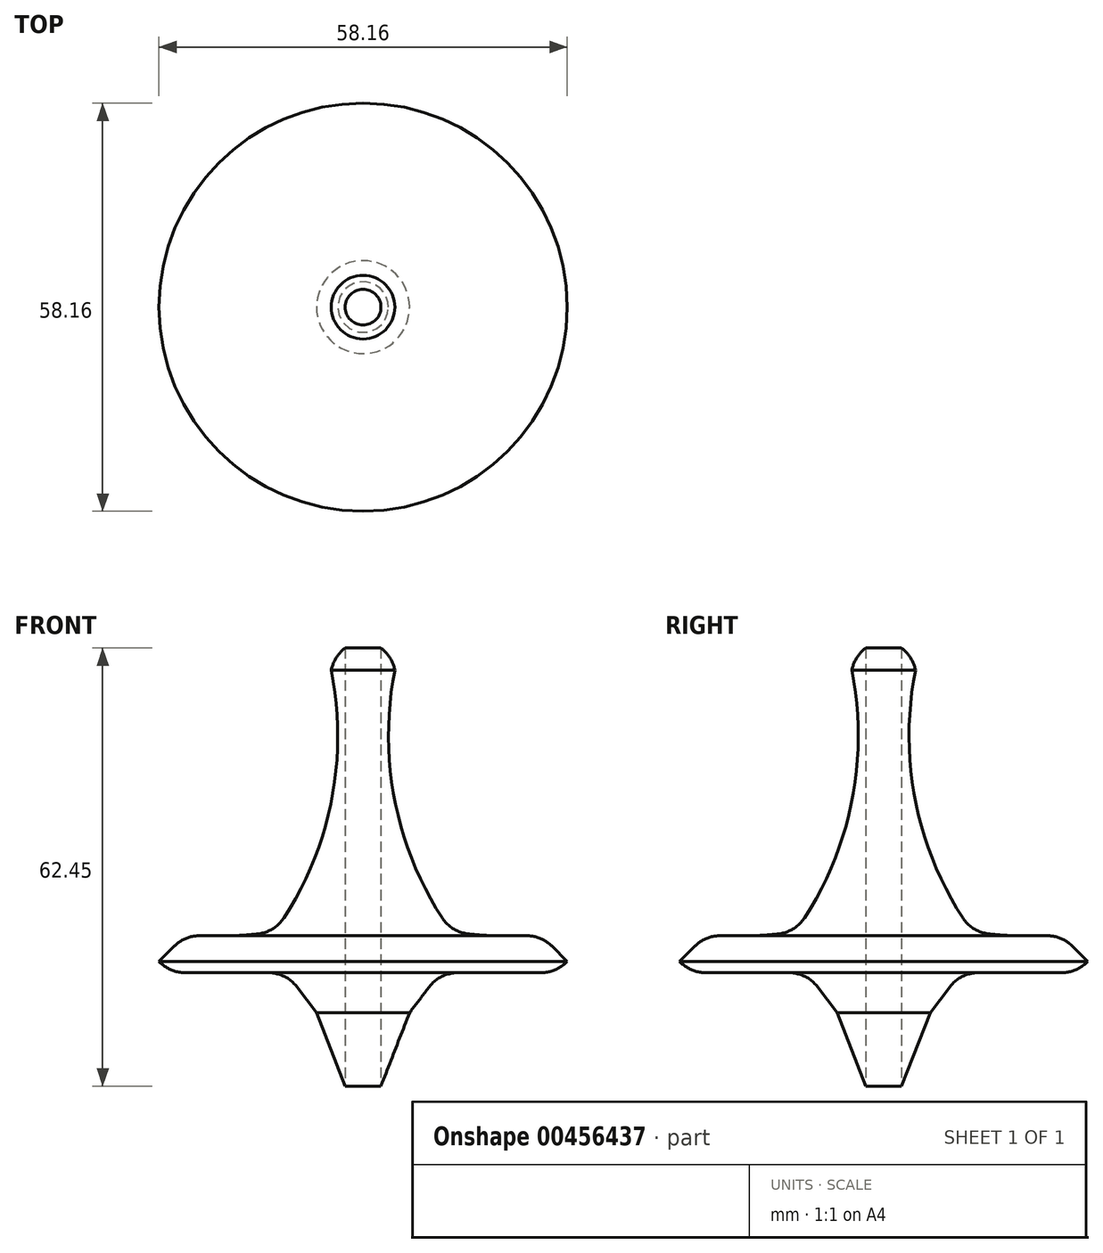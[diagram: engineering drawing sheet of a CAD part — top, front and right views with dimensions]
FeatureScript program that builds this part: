
annotation { "Feature Type Name" : "Feature", "Feature Type Description" : "" }
export const myFeature = defineFeature(function(context is Context, id is Id, definition is map)
    precondition{}
    {
        {
            var Q0;
            Q0=qCreatedBy(makeId("Front.planeOp"),FACE);
            var sketch = newSketch(context, id + "F0", { "sketchPlane" : qUnion([Q0])});
            skLineSegment(sketch, "E0", {"start": v(0, 63.5) * mm, "end": v(0, 0) * mm});
            skArc(sketch, "E1", {"start": v(12.6, 22.03) * mm, "mid": v(16.63, 21.53) * mm, "end": v(20.7, 21.42) * mm});
            skArc(sketch, "E2", {"start": v(4.53, 59.28) * mm, "mid": v(4.7, 39.82) * mm, "end": v(12.6, 22.03) * mm});
            skArc(sketch, "E3", {"start": v(4.53, 59.28) * mm, "mid": v(2.94, 62.12) * mm, "end": v(0, 63.5) * mm});
            skLineSegment(sketch, "E4", {"start": v(30.48, 16.15) * mm, "end": v(10.96, 16.15) * mm});
            skPoint(sketch, "E5.end.orphan", {"position": v(10.96, 17.31) * mm});
            skPoint(sketch, "E6", {"position": v(20.7, 21.42) * mm});
            skLineSegment(sketch, "E7", {"start": v(0, 0) * mm, "end": v(2.55, 0) * mm});
            skLineSegment(sketch, "E8", {"start": v(2.55, 0) * mm, "end": v(6.63, 10.45) * mm});
            skLineSegment(sketch, "E9", {"start": v(6.63, 10.45) * mm, "end": v(10.96, 16.15) * mm});
            skPoint(sketch, "E10.center.orphan", {"position": v(25.93, 21.42) * mm});
            skLineSegment(sketch, "E11", {"start": v(20.7, 21.42) * mm, "end": v(30.43, 21.42) * mm});
            skLineSegment(sketch, "E12", {"start": v(30.43, 21.42) * mm, "end": v(30.48, 16.15) * mm});
            skSolve(sketch);
        }
        {
            var Q0;
            Q0=qSketchRegion(id+"F0",true);
            var Q1;
            Q1=sQuery(id+"F0.wireOp",EDGE,"E0");
            revolve(context, id + "F1", {"entities" : qUnion([Q0]), "axis" : qUnion([Q1]), "revolveType" : RevolveType.FULL});
        }
        {
            var Q0;
            Q0=makeQuery(id+"F1.opRevolve","SWEPT_FACE",FACE,{"disambiguationData":[OSD([sQuery(id+"F0.wireOp",EDGE,"E7")])]});
            extrude(context, id + "F2", {"entities" : qUnion([Q0]), "operationType" : NewBodyOperationType.REMOVE, "endBound" : BoundingType.THROUGH_ALL, "oppositeDirection" : true, "depth" : 25.4 * mm});
        }
        {
            var Q0;
            Q0=makeQuery(id+"F1.opRevolve","SWEPT_FACE",FACE,{"disambiguationData":[OSD([sQuery(id+"F0.wireOp",EDGE,"E4")])]});
            fillet(context, id + "F3", {"entities" : qUnion([Q0]), "radius" : 5.08 * mm, "tangentPropagation" : true, "allowEdgeOverflow" : false});
        }
        {
            var Q0;
            Q0=makeQuery(id+"F1.opRevolve","SWEPT_EDGE",EDGE,{"disambiguationData":[OSD([sQuery(id+"F0.wireOp",EDGE,"E11"),sQuery(id+"F0.wireOp",EDGE,"E12")])]});
            chamfer(context, id + "F4", {"entities" : qUnion([Q0]), "width" : 5.08 * mm, "tangentPropagation" : true});
        }
        {
            var Q0;
            Q0=makeQuery(id+"F1.opRevolve","SWEPT_FACE",FACE,{"disambiguationData":[OSD([sQuery(id+"F0.wireOp",EDGE,"E1")])]});
            fillet(context, id + "F5", {"entities" : qUnion([Q0]), "radius" : 5.08 * mm, "tangentPropagation" : true, "allowEdgeOverflow" : false});
        }
        {
            var Q0;
            Q0=makeQuery(id+"F1.opRevolve","SWEPT_FACE",FACE,{"disambiguationData":[OSD([sQuery(id+"F0.wireOp",EDGE,"E11")])]});
            fillet(context, id + "F6", {"entities" : qUnion([Q0]), "radius" : 5.08 * mm, "tangentPropagation" : true, "allowEdgeOverflow" : false});
        }
    });
